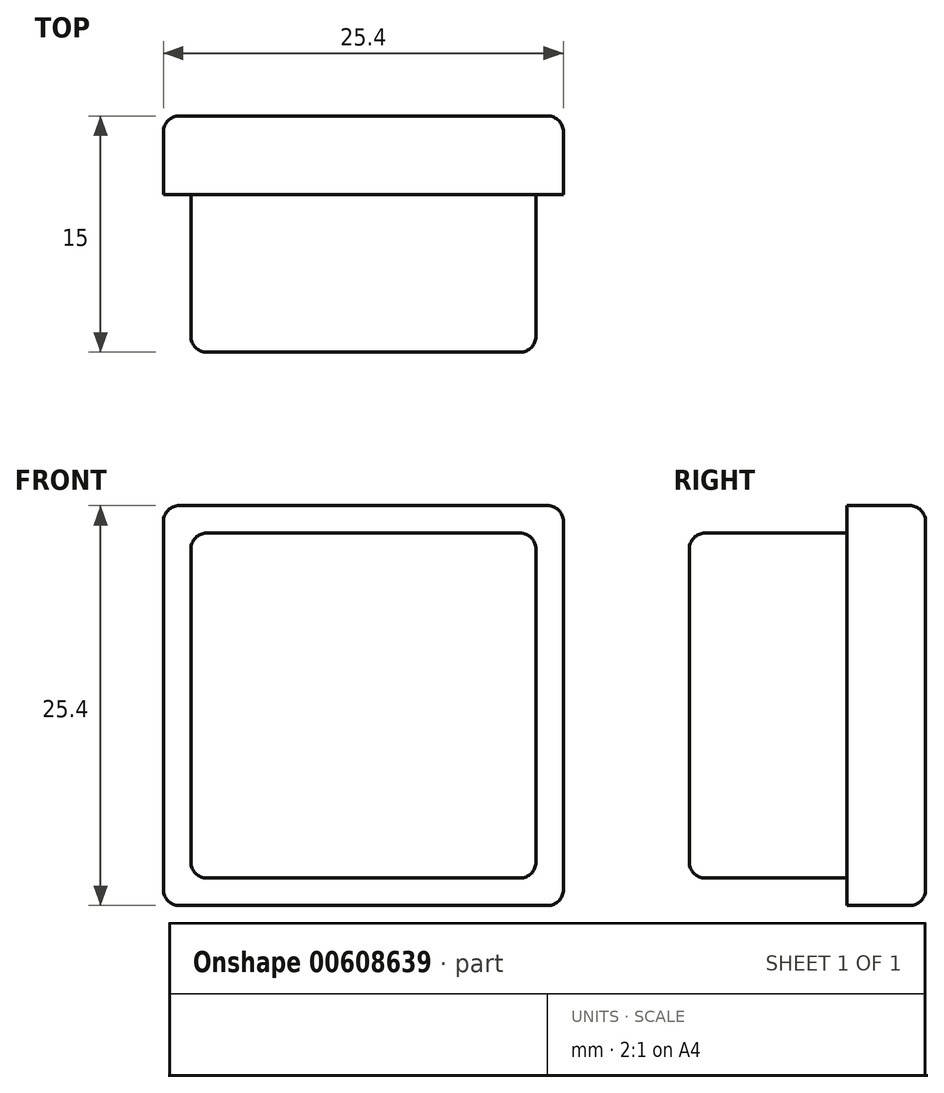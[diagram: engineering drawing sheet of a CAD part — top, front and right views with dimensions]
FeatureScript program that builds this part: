
annotation { "Feature Type Name" : "Feature", "Feature Type Description" : "" }
export const myFeature = defineFeature(function(context is Context, id is Id, definition is map)
    precondition{}
    {
        {
            assignVariable(context, id + "F0", {"name" : "aboveHeight", "anyValue" : 5});
        }
        {
            assignVariable(context, id + "F1", {"name" : "belowHeight", "anyValue" : 10});
        }
        {
            var Q0;
            Q0=qCreatedBy(makeId("Front.planeOp"),FACE);
            var sketch = newSketch(context, id + "F2", { "sketchPlane" : qUnion([Q0])});
            skLineSegment(sketch, "E0.bottom", {"start": v(12.7, 12.7) * mm, "end": v(-12.7, 12.7) * mm});
            skLineSegment(sketch, "E0.top", {"start": v(12.7, -12.7) * mm, "end": v(-12.7, -12.7) * mm});
            skLineSegment(sketch, "E0.left", {"start": v(12.7, 12.7) * mm, "end": v(12.7, -12.7) * mm});
            skLineSegment(sketch, "E0.right", {"start": v(-12.7, 12.7) * mm, "end": v(-12.7, -12.7) * mm});
            skPoint(sketch, "E0.middle", {"position": v(0, 0) * mm});
            skSolve(sketch);
        }
        {
            var Q0;
            Q0=makeQuery(id+"F2.imprint","IMPRINT",FACE,{"disambiguationData":[TD([[makeQuery(id+"F2.imprint","IMPRINT",EDGE,{"derivedFrom":sQuery(id+"F2.wireOp",EDGE,"E0.bottom")}),1.0]])]});
            extrude(context, id + "F3", {"entities" : qUnion([Q0]), "depth" : (getVariable(context, 'aboveHeight')) * mm, "offsetDistance" : 25 * mm});
        }
        {
            var Q0;
            Q0=makeQuery(id+"F3.opExtrude","CAP_FACE",FACE,{"disambiguationData":[OSD([sQuery(id+"F2.wireOp",EDGE,"E0.bottom"),sQuery(id+"F2.wireOp",EDGE,"E0.top"),sQuery(id+"F2.wireOp",EDGE,"E0.left"),sQuery(id+"F2.wireOp",EDGE,"E0.right")])],"isStart":false});
            var sketch = newSketch(context, id + "F4", { "sketchPlane" : qUnion([Q0])});
            skLineSegment(sketch, "E1.bottom", {"start": v(10.95, 10.95) * mm, "end": v(-10.95, 10.95) * mm});
            skLineSegment(sketch, "E1.top", {"start": v(10.95, -10.95) * mm, "end": v(-10.95, -10.95) * mm});
            skLineSegment(sketch, "E1.left", {"start": v(10.95, 10.95) * mm, "end": v(10.95, -10.95) * mm});
            skLineSegment(sketch, "E1.right", {"start": v(-10.95, 10.95) * mm, "end": v(-10.95, -10.95) * mm});
            skPoint(sketch, "E1.middle", {"position": v(0, 0) * mm});
            skSolve(sketch);
        }
        {
            var Q0;
            Q0=makeQuery(id+"F4.imprint","IMPRINT",FACE,{"disambiguationData":[TD([[makeQuery(id+"F4.imprint","IMPRINT",EDGE,{"derivedFrom":sQuery(id+"F4.wireOp",EDGE,"E1.bottom")}),1.0]])]});
            extrude(context, id + "F5", {"entities" : qUnion([Q0]), "operationType" : NewBodyOperationType.ADD, "depth" : (getVariable(context, 'belowHeight')) * mm, "offsetDistance" : 25 * mm});
        }
        {
            var Q0;
            Q0=makeQuery(id+"F5.opExtrude","CAP_EDGE",EDGE,{"disambiguationData":[OSD([sQuery(id+"F4.wireOp",EDGE,"E1.bottom")])],"isStart":false});
            var Q1;
            Q1=makeQuery(id+"F5.opExtrude","SWEPT_EDGE",EDGE,{"disambiguationData":[OSD([sQuery(id+"F4.wireOp",EDGE,"E1.bottom"),sQuery(id+"F4.wireOp",EDGE,"E1.left")])]});
            var Q2;
            Q2=makeQuery(id+"F5.opExtrude","CAP_EDGE",EDGE,{"disambiguationData":[OSD([sQuery(id+"F4.wireOp",EDGE,"E1.left")])],"isStart":false});
            var Q3;
            Q3=makeQuery(id+"F3.opExtrude","CAP_EDGE",EDGE,{"disambiguationData":[OSD([sQuery(id+"F2.wireOp",EDGE,"E0.left")])],"isStart":true});
            var Q4;
            Q4=makeQuery(id+"F3.opExtrude","SWEPT_EDGE",EDGE,{"disambiguationData":[OSD([sQuery(id+"F2.wireOp",EDGE,"E0.bottom"),sQuery(id+"F2.wireOp",EDGE,"E0.left")])]});
            var Q5;
            Q5=makeQuery(id+"F3.opExtrude","CAP_EDGE",EDGE,{"disambiguationData":[OSD([sQuery(id+"F2.wireOp",EDGE,"E0.bottom")])],"isStart":true});
            var Q6;
            Q6=makeQuery(id+"F3.opExtrude","SWEPT_EDGE",EDGE,{"disambiguationData":[OSD([sQuery(id+"F2.wireOp",EDGE,"E0.bottom"),sQuery(id+"F2.wireOp",EDGE,"E0.right")])]});
            var Q7;
            Q7=makeQuery(id+"F3.opExtrude","CAP_EDGE",EDGE,{"disambiguationData":[OSD([sQuery(id+"F2.wireOp",EDGE,"E0.right")])],"isStart":true});
            var Q8;
            Q8=makeQuery(id+"F5.opExtrude","SWEPT_EDGE",EDGE,{"disambiguationData":[OSD([sQuery(id+"F4.wireOp",EDGE,"E1.bottom"),sQuery(id+"F4.wireOp",EDGE,"E1.right")])]});
            var Q9;
            Q9=makeQuery(id+"F5.opExtrude","CAP_EDGE",EDGE,{"disambiguationData":[OSD([sQuery(id+"F4.wireOp",EDGE,"E1.right")])],"isStart":false});
            var Q10;
            Q10=makeQuery(id+"F3.opExtrude","SWEPT_EDGE",EDGE,{"disambiguationData":[OSD([sQuery(id+"F2.wireOp",EDGE,"E0.top"),sQuery(id+"F2.wireOp",EDGE,"E0.right")])]});
            var Q11;
            Q11=makeQuery(id+"F3.opExtrude","CAP_EDGE",EDGE,{"disambiguationData":[OSD([sQuery(id+"F2.wireOp",EDGE,"E0.top")])],"isStart":true});
            var Q12;
            Q12=makeQuery(id+"F3.opExtrude","SWEPT_EDGE",EDGE,{"disambiguationData":[OSD([sQuery(id+"F2.wireOp",EDGE,"E0.top"),sQuery(id+"F2.wireOp",EDGE,"E0.left")])]});
            var Q13;
            Q13=makeQuery(id+"F5.opExtrude","SWEPT_EDGE",EDGE,{"disambiguationData":[OSD([sQuery(id+"F4.wireOp",EDGE,"E1.top"),sQuery(id+"F4.wireOp",EDGE,"E1.right")])]});
            var Q14;
            Q14=makeQuery(id+"F5.opExtrude","CAP_EDGE",EDGE,{"disambiguationData":[OSD([sQuery(id+"F4.wireOp",EDGE,"E1.top")])],"isStart":false});
            var Q15;
            Q15=makeQuery(id+"F5.opExtrude","SWEPT_EDGE",EDGE,{"disambiguationData":[OSD([sQuery(id+"F4.wireOp",EDGE,"E1.top"),sQuery(id+"F4.wireOp",EDGE,"E1.left")])]});
            fillet(context, id + "F6", {"entities" : qUnion([Q0, Q1, Q2, Q3, Q4, Q5, Q6, Q7, Q8, Q9, Q10, Q11, Q12, Q13, Q14, Q15]), "radius" : 1 * mm, "tangentPropagation" : true, "allowEdgeOverflow" : false});
        }
    });
